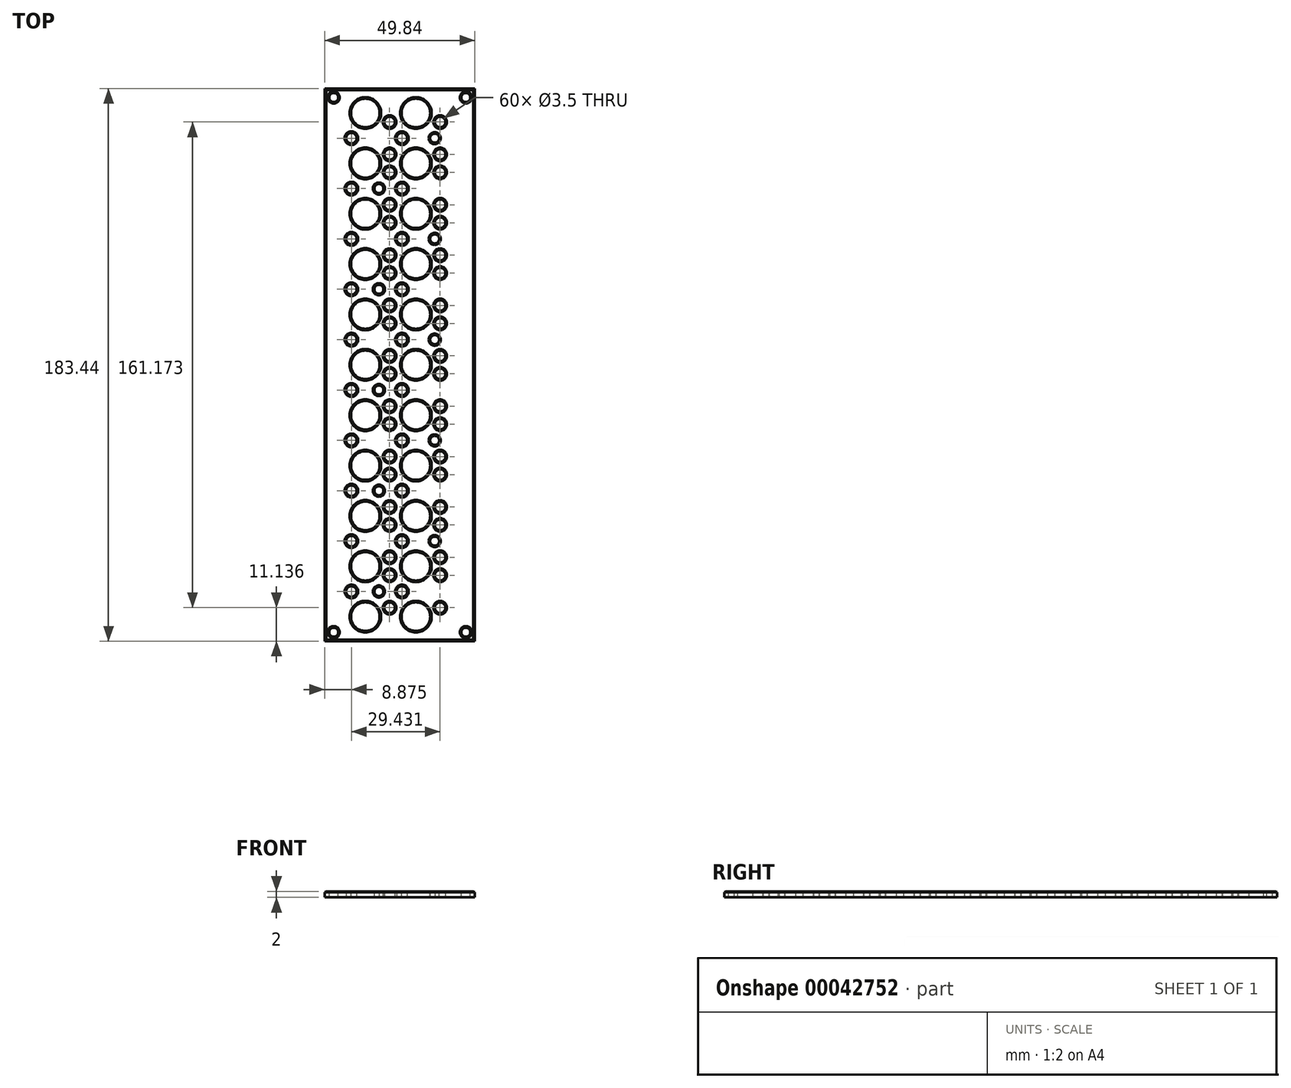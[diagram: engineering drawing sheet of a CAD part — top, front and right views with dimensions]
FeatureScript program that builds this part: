
annotation { "Feature Type Name" : "Feature", "Feature Type Description" : "" }
export const myFeature = defineFeature(function(context is Context, id is Id, definition is map)
    precondition{}
    {
        {
            var Q0;
            Q0=qCreatedBy(makeId("Top.planeOp"),FACE);
            var sketch = newSketch(context, id + "F0", { "sketchPlane" : qUnion([Q0])});
            skLineSegment(sketch, "E0.right", {"start": v(46.84, -3) * mm, "end": v(46.84, 180.44) * mm});
            skLineSegment(sketch, "E0.left", {"start": v(-3, -3) * mm, "end": v(-3, 180.44) * mm});
            skLineSegment(sketch, "E0.top", {"start": v(-3, 180.44) * mm, "end": v(46.84, 180.44) * mm});
            skLineSegment(sketch, "E0.bottom", {"start": v(-3, -3) * mm, "end": v(46.84, -3) * mm});
            skPoint(sketch, "E1.rect.middle", {"position": v(5.88, 30.23) * mm});
            skPoint(sketch, "E2.rect.middle", {"position": v(35.3, 8.14) * mm});
            skPoint(sketch, "E3.rect.middle", {"position": v(35.3, 24.85) * mm});
            skPoint(sketch, "E4.rect.middle", {"position": v(18.54, 24.85) * mm});
            skPoint(sketch, "E5.rect.middle", {"position": v(35.3, 18.89) * mm});
            skPoint(sketch, "E6.rect.middle", {"position": v(22.64, 13.51) * mm});
            skPoint(sketch, "E7.rect.middle", {"position": v(35.3, 35.6) * mm});
            skPoint(sketch, "E8.rect.middle", {"position": v(18.54, 8.14) * mm});
            skPoint(sketch, "E9.rect.middle", {"position": v(18.54, 35.6) * mm});
            skPoint(sketch, "E10.rect.middle", {"position": v(5.88, 13.51) * mm});
            skPoint(sketch, "E11.rect.middle", {"position": v(22.64, 30.23) * mm});
            skPoint(sketch, "E12.rect.middle", {"position": v(18.54, 18.89) * mm});
            skCircle(sketch, "E13", {"center": v(5.88, 13.51) * mm, "radius": 1.75 * mm});
            skCircle(sketch, "E14", {"center": v(18.54, 8.14) * mm, "radius": 1.75 * mm});
            skCircle(sketch, "E15", {"center": v(18.54, 18.89) * mm, "radius": 1.75 * mm});
            skCircle(sketch, "E16", {"center": v(22.64, 13.51) * mm, "radius": 1.75 * mm});
            skCircle(sketch, "E17", {"center": v(35.3, 8.14) * mm, "radius": 1.75 * mm});
            skCircle(sketch, "E18", {"center": v(35.3, 18.89) * mm, "radius": 1.75 * mm});
            skCircle(sketch, "E19", {"center": v(35.3, 24.85) * mm, "radius": 1.75 * mm});
            skCircle(sketch, "E20", {"center": v(35.3, 35.6) * mm, "radius": 1.75 * mm});
            skCircle(sketch, "E21", {"center": v(22.64, 30.23) * mm, "radius": 1.75 * mm});
            skCircle(sketch, "E22", {"center": v(18.54, 35.6) * mm, "radius": 1.75 * mm});
            skCircle(sketch, "E23", {"center": v(18.54, 24.85) * mm, "radius": 1.75 * mm});
            skCircle(sketch, "E24", {"center": v(5.88, 30.23) * mm, "radius": 1.75 * mm});
            skPoint(sketch, "E25.rect.middle", {"position": v(18.54, 69.03) * mm});
            skPoint(sketch, "E26.rect.middle", {"position": v(35.3, 41.56) * mm});
            skPoint(sketch, "E27.rect.middle", {"position": v(35.3, 52.32) * mm});
            skPoint(sketch, "E28.rect.middle", {"position": v(5.88, 46.94) * mm});
            skPoint(sketch, "E29.rect.middle", {"position": v(18.54, 52.32) * mm});
            skPoint(sketch, "E30.rect.middle", {"position": v(35.3, 69.03) * mm});
            skPoint(sketch, "E31.rect.middle", {"position": v(18.54, 41.56) * mm});
            skPoint(sketch, "E32.rect.middle", {"position": v(5.88, 63.65) * mm});
            skPoint(sketch, "E33.rect.middle", {"position": v(35.3, 58.28) * mm});
            skPoint(sketch, "E34.rect.middle", {"position": v(18.54, 58.28) * mm});
            skCircle(sketch, "E35", {"center": v(18.54, 41.56) * mm, "radius": 1.75 * mm});
            skCircle(sketch, "E36", {"center": v(35.3, 41.56) * mm, "radius": 1.75 * mm});
            skCircle(sketch, "E37", {"center": v(35.3, 52.32) * mm, "radius": 1.75 * mm});
            skCircle(sketch, "E38", {"center": v(35.3, 69.03) * mm, "radius": 1.75 * mm});
            skPoint(sketch, "E39.rect.middle", {"position": v(22.64, 63.65) * mm});
            skCircle(sketch, "E40", {"center": v(18.54, 69.03) * mm, "radius": 1.75 * mm});
            skPoint(sketch, "E41.rect.middle", {"position": v(22.64, 46.94) * mm});
            skCircle(sketch, "E42", {"center": v(18.54, 58.28) * mm, "radius": 1.75 * mm});
            skCircle(sketch, "E43", {"center": v(5.88, 63.65) * mm, "radius": 1.75 * mm});
            skCircle(sketch, "E44", {"center": v(5.88, 46.94) * mm, "radius": 1.75 * mm});
            skCircle(sketch, "E45", {"center": v(18.54, 52.32) * mm, "radius": 1.75 * mm});
            skCircle(sketch, "E46", {"center": v(35.3, 58.28) * mm, "radius": 1.75 * mm});
            skCircle(sketch, "E47", {"center": v(22.64, 63.65) * mm, "radius": 1.75 * mm});
            skCircle(sketch, "E48", {"center": v(22.64, 46.94) * mm, "radius": 1.75 * mm});
            skCircle(sketch, "E49", {"center": v(18.54, 135.88) * mm, "radius": 1.75 * mm});
            skPoint(sketch, "E50.rect.middle", {"position": v(35.3, 74.99) * mm});
            skPoint(sketch, "E51.rect.middle", {"position": v(22.64, 130.5) * mm});
            skPoint(sketch, "E52.rect.middle", {"position": v(35.3, 135.88) * mm});
            skPoint(sketch, "E53.rect.middle", {"position": v(5.88, 80.37) * mm});
            skCircle(sketch, "E54", {"center": v(18.54, 125.13) * mm, "radius": 1.75 * mm});
            skCircle(sketch, "E55", {"center": v(18.54, 119.17) * mm, "radius": 1.75 * mm});
            skCircle(sketch, "E56", {"center": v(35.3, 108.42) * mm, "radius": 1.75 * mm});
            skPoint(sketch, "E57.rect.middle", {"position": v(35.3, 125.13) * mm});
            skCircle(sketch, "E58", {"center": v(35.3, 125.13) * mm, "radius": 1.75 * mm});
            skCircle(sketch, "E59", {"center": v(35.3, 119.17) * mm, "radius": 1.75 * mm});
            skCircle(sketch, "E60", {"center": v(35.3, 74.99) * mm, "radius": 1.75 * mm});
            skPoint(sketch, "E61.rect.middle", {"position": v(5.88, 97.08) * mm});
            skCircle(sketch, "E62", {"center": v(22.64, 80.37) * mm, "radius": 1.75 * mm});
            skCircle(sketch, "E63", {"center": v(18.54, 85.74) * mm, "radius": 1.75 * mm});
            skPoint(sketch, "E64.rect.middle", {"position": v(18.54, 102.46) * mm});
            skPoint(sketch, "E65.rect.middle", {"position": v(22.64, 113.8) * mm});
            skCircle(sketch, "E66", {"center": v(18.54, 74.99) * mm, "radius": 1.75 * mm});
            skCircle(sketch, "E67", {"center": v(18.54, 91.7) * mm, "radius": 1.75 * mm});
            skCircle(sketch, "E68", {"center": v(5.88, 80.37) * mm, "radius": 1.75 * mm});
            skCircle(sketch, "E69", {"center": v(5.88, 97.08) * mm, "radius": 1.75 * mm});
            skPoint(sketch, "E70.rect.middle", {"position": v(35.3, 102.46) * mm});
            skCircle(sketch, "E71", {"center": v(18.54, 102.46) * mm, "radius": 1.75 * mm});
            skCircle(sketch, "E72", {"center": v(35.3, 135.88) * mm, "radius": 1.75 * mm});
            skCircle(sketch, "E73", {"center": v(22.64, 130.5) * mm, "radius": 1.75 * mm});
            skPoint(sketch, "E74.rect.middle", {"position": v(5.88, 113.8) * mm});
            skCircle(sketch, "E75", {"center": v(35.3, 85.74) * mm, "radius": 1.75 * mm});
            skPoint(sketch, "E76.rect.middle", {"position": v(18.54, 108.42) * mm});
            skPoint(sketch, "E77.rect.middle", {"position": v(22.64, 97.08) * mm});
            skCircle(sketch, "E78", {"center": v(5.88, 130.5) * mm, "radius": 1.75 * mm});
            skPoint(sketch, "E79.rect.middle", {"position": v(35.3, 91.7) * mm});
            skCircle(sketch, "E80", {"center": v(35.3, 91.7) * mm, "radius": 1.75 * mm});
            skCircle(sketch, "E81", {"center": v(35.3, 102.46) * mm, "radius": 1.75 * mm});
            skCircle(sketch, "E82", {"center": v(22.64, 97.08) * mm, "radius": 1.75 * mm});
            skCircle(sketch, "E83", {"center": v(22.64, 113.8) * mm, "radius": 1.75 * mm});
            skCircle(sketch, "E84", {"center": v(5.88, 113.8) * mm, "radius": 1.75 * mm});
            skCircle(sketch, "E85", {"center": v(18.54, 108.42) * mm, "radius": 1.75 * mm});
            skPoint(sketch, "E86.rect.middle", {"position": v(5.88, 147.22) * mm});
            skPoint(sketch, "E87.rect.middle", {"position": v(18.54, 152.6) * mm});
            skPoint(sketch, "E88.rect.middle", {"position": v(35.3, 169.3) * mm});
            skPoint(sketch, "E89.rect.middle", {"position": v(35.3, 141.84) * mm});
            skPoint(sketch, "E90.rect.middle", {"position": v(18.54, 141.84) * mm});
            skPoint(sketch, "E91.rect.middle", {"position": v(18.54, 169.3) * mm});
            skPoint(sketch, "E92.rect.middle", {"position": v(35.3, 152.6) * mm});
            skPoint(sketch, "E93.rect.middle", {"position": v(18.54, 158.56) * mm});
            skPoint(sketch, "E94.rect.middle", {"position": v(35.3, 158.56) * mm});
            skPoint(sketch, "E95.rect.middle", {"position": v(5.88, 163.93) * mm});
            skCircle(sketch, "E96", {"center": v(35.3, 141.84) * mm, "radius": 1.75 * mm});
            skCircle(sketch, "E97", {"center": v(35.3, 169.3) * mm, "radius": 1.75 * mm});
            skCircle(sketch, "E98", {"center": v(5.88, 163.93) * mm, "radius": 1.75 * mm});
            skCircle(sketch, "E99", {"center": v(18.54, 158.56) * mm, "radius": 1.75 * mm});
            skCircle(sketch, "E100", {"center": v(35.3, 158.56) * mm, "radius": 1.75 * mm});
            skCircle(sketch, "E101", {"center": v(35.3, 152.6) * mm, "radius": 1.75 * mm});
            skCircle(sketch, "E102", {"center": v(18.54, 169.3) * mm, "radius": 1.75 * mm});
            skCircle(sketch, "E103", {"center": v(5.88, 147.22) * mm, "radius": 1.75 * mm});
            skPoint(sketch, "E104.rect.middle", {"position": v(22.64, 147.22) * mm});
            skCircle(sketch, "E105", {"center": v(18.54, 152.6) * mm, "radius": 1.75 * mm});
            skCircle(sketch, "E106", {"center": v(18.54, 141.84) * mm, "radius": 1.75 * mm});
            skPoint(sketch, "E107.rect.middle", {"position": v(22.64, 163.93) * mm});
            skCircle(sketch, "E108", {"center": v(22.64, 147.22) * mm, "radius": 1.75 * mm});
            skCircle(sketch, "E109", {"center": v(22.64, 163.93) * mm, "radius": 1.75 * mm});
            skSolve(sketch);
        }
        {
            var Q0;
            Q0=qSketchRegion(id+"F0",true);
            extrude(context, id + "F1", {"entities" : qUnion([Q0]), "depth" : 2 * mm});
        }
        {
            var Q0;
            Q0=makeQuery(id+"F1.opExtrude","CAP_FACE",FACE,{"disambiguationData":[OSD([sQuery(id+"F0.wireOp",EDGE,"E0.right"),sQuery(id+"F0.wireOp",EDGE,"E0.left"),sQuery(id+"F0.wireOp",EDGE,"E0.top"),sQuery(id+"F0.wireOp",EDGE,"E0.bottom"),sQuery(id+"F0.wireOp",EDGE,"E13"),sQuery(id+"F0.wireOp",EDGE,"E14"),sQuery(id+"F0.wireOp",EDGE,"E15"),sQuery(id+"F0.wireOp",EDGE,"E16"),sQuery(id+"F0.wireOp",EDGE,"E17"),sQuery(id+"F0.wireOp",EDGE,"E18"),sQuery(id+"F0.wireOp",EDGE,"E19"),sQuery(id+"F0.wireOp",EDGE,"E20"),sQuery(id+"F0.wireOp",EDGE,"E21"),sQuery(id+"F0.wireOp",EDGE,"E22"),sQuery(id+"F0.wireOp",EDGE,"E23"),sQuery(id+"F0.wireOp",EDGE,"E24"),sQuery(id+"F0.wireOp",EDGE,"E35"),sQuery(id+"F0.wireOp",EDGE,"E36"),sQuery(id+"F0.wireOp",EDGE,"E37"),sQuery(id+"F0.wireOp",EDGE,"E38"),sQuery(id+"F0.wireOp",EDGE,"E40"),sQuery(id+"F0.wireOp",EDGE,"E42"),sQuery(id+"F0.wireOp",EDGE,"E43"),sQuery(id+"F0.wireOp",EDGE,"E44"),sQuery(id+"F0.wireOp",EDGE,"E45"),sQuery(id+"F0.wireOp",EDGE,"E46"),sQuery(id+"F0.wireOp",EDGE,"E47"),sQuery(id+"F0.wireOp",EDGE,"E48"),sQuery(id+"F0.wireOp",EDGE,"E49"),sQuery(id+"F0.wireOp",EDGE,"E54"),sQuery(id+"F0.wireOp",EDGE,"E55"),sQuery(id+"F0.wireOp",EDGE,"E56"),sQuery(id+"F0.wireOp",EDGE,"E58"),sQuery(id+"F0.wireOp",EDGE,"E59"),sQuery(id+"F0.wireOp",EDGE,"E60"),sQuery(id+"F0.wireOp",EDGE,"E62"),sQuery(id+"F0.wireOp",EDGE,"E63"),sQuery(id+"F0.wireOp",EDGE,"E66"),sQuery(id+"F0.wireOp",EDGE,"E67"),sQuery(id+"F0.wireOp",EDGE,"E68"),sQuery(id+"F0.wireOp",EDGE,"E69"),sQuery(id+"F0.wireOp",EDGE,"E71"),sQuery(id+"F0.wireOp",EDGE,"E72"),sQuery(id+"F0.wireOp",EDGE,"E73"),sQuery(id+"F0.wireOp",EDGE,"E75"),sQuery(id+"F0.wireOp",EDGE,"E78"),sQuery(id+"F0.wireOp",EDGE,"E80"),sQuery(id+"F0.wireOp",EDGE,"E81"),sQuery(id+"F0.wireOp",EDGE,"E82"),sQuery(id+"F0.wireOp",EDGE,"E83"),sQuery(id+"F0.wireOp",EDGE,"E84"),sQuery(id+"F0.wireOp",EDGE,"E85"),sQuery(id+"F0.wireOp",EDGE,"E96"),sQuery(id+"F0.wireOp",EDGE,"E97"),sQuery(id+"F0.wireOp",EDGE,"E98"),sQuery(id+"F0.wireOp",EDGE,"E99"),sQuery(id+"F0.wireOp",EDGE,"E100"),sQuery(id+"F0.wireOp",EDGE,"E101"),sQuery(id+"F0.wireOp",EDGE,"E102"),sQuery(id+"F0.wireOp",EDGE,"E103"),sQuery(id+"F0.wireOp",EDGE,"E105"),sQuery(id+"F0.wireOp",EDGE,"E106"),sQuery(id+"F0.wireOp",EDGE,"E108"),sQuery(id+"F0.wireOp",EDGE,"E109")])],"isStart":false});
            var sketch = newSketch(context, id + "F2", { "sketchPlane" : qUnion([Q0])});
            skCircle(sketch, "E110", {"center": v(10.5, 21.87) * mm, "radius": 4.75 * mm});
            skCircle(sketch, "E111", {"center": v(10.5, 138.86) * mm, "radius": 4.75 * mm});
            skCircle(sketch, "E112", {"center": v(27.26, 155.58) * mm, "radius": 4.75 * mm});
            skCircle(sketch, "E113", {"center": v(27.26, 122.15) * mm, "radius": 4.75 * mm});
            skCircle(sketch, "E114", {"center": v(27.26, 38.58) * mm, "radius": 4.75 * mm});
            skCircle(sketch, "E115", {"center": v(10.5, 155.58) * mm, "radius": 4.75 * mm});
            skCircle(sketch, "E116", {"center": v(10.5, 105.44) * mm, "radius": 4.75 * mm});
            skCircle(sketch, "E117", {"center": v(27.26, 105.44) * mm, "radius": 4.75 * mm});
            skCircle(sketch, "E118", {"center": v(10.5, 88.72) * mm, "radius": 4.75 * mm});
            skCircle(sketch, "E119", {"center": v(27.26, 88.72) * mm, "radius": 4.75 * mm});
            skCircle(sketch, "E120", {"center": v(10.5, 122.15) * mm, "radius": 4.75 * mm});
            skCircle(sketch, "E121", {"center": v(27.26, 172.29) * mm, "radius": 4.75 * mm});
            skCircle(sketch, "E122", {"center": v(10.5, 5.16) * mm, "radius": 4.75 * mm});
            skCircle(sketch, "E123", {"center": v(27.26, 5.16) * mm, "radius": 4.75 * mm});
            skCircle(sketch, "E124", {"center": v(27.26, 21.87) * mm, "radius": 4.75 * mm});
            skCircle(sketch, "E125", {"center": v(27.26, 55.3) * mm, "radius": 4.75 * mm});
            skCircle(sketch, "E126", {"center": v(10.5, 38.58) * mm, "radius": 4.75 * mm});
            skCircle(sketch, "E127", {"center": v(10.5, 172.29) * mm, "radius": 4.75 * mm});
            skCircle(sketch, "E128", {"center": v(27.26, 72) * mm, "radius": 4.75 * mm});
            skCircle(sketch, "E129", {"center": v(10.5, 55.3) * mm, "radius": 4.75 * mm});
            skCircle(sketch, "E130", {"center": v(27.26, 138.86) * mm, "radius": 4.75 * mm});
            skCircle(sketch, "E131", {"center": v(10.5, 72) * mm, "radius": 4.75 * mm});
            skCircle(sketch, "E132", {"center": v(43.84, 0) * mm, "radius": 1.5 * mm});
            skCircle(sketch, "E133", {"center": v(0, 177.44) * mm, "radius": 1.5 * mm});
            skCircle(sketch, "E134", {"center": v(15, 13.51) * mm, "radius": 1.5 * mm});
            skCircle(sketch, "E135", {"center": v(33.5, 30.23) * mm, "radius": 1.5 * mm});
            skCircle(sketch, "E136", {"center": v(15, 46.94) * mm, "radius": 1.5 * mm});
            skCircle(sketch, "E137", {"center": v(33.5, 63.65) * mm, "radius": 1.5 * mm});
            skCircle(sketch, "E138", {"center": v(15, 80.37) * mm, "radius": 1.5 * mm});
            skCircle(sketch, "E139", {"center": v(33.5, 97.08) * mm, "radius": 1.5 * mm});
            skCircle(sketch, "E140", {"center": v(15, 113.8) * mm, "radius": 1.5 * mm});
            skCircle(sketch, "E141", {"center": v(33.5, 130.5) * mm, "radius": 1.5 * mm});
            skCircle(sketch, "E142", {"center": v(33.5, 163.93) * mm, "radius": 1.5 * mm});
            skCircle(sketch, "E143", {"center": v(15, 147.22) * mm, "radius": 1.5 * mm});
            skCircle(sketch, "E144", {"center": v(0, 0) * mm, "radius": 1.5 * mm});
            skCircle(sketch, "E145", {"center": v(43.84, 177.44) * mm, "radius": 1.5 * mm});
            skSolve(sketch);
        }
        {
            var Q0;
            Q0=qSketchRegion(id+"F2",true);
            extrude(context, id + "F3", {"entities" : qUnion([Q0]), "operationType" : NewBodyOperationType.REMOVE, "oppositeDirection" : true, "depth" : 25 * mm});
        }
        {
            var Q0;
            Q0=makeQuery(id+"F1.opExtrude","CAP_FACE",FACE,{"disambiguationData":[OSD([sQuery(id+"F0.wireOp",EDGE,"E0.right"),sQuery(id+"F0.wireOp",EDGE,"E0.left"),sQuery(id+"F0.wireOp",EDGE,"E0.top"),sQuery(id+"F0.wireOp",EDGE,"E0.bottom"),sQuery(id+"F0.wireOp",EDGE,"E13"),sQuery(id+"F0.wireOp",EDGE,"E14"),sQuery(id+"F0.wireOp",EDGE,"E15"),sQuery(id+"F0.wireOp",EDGE,"E16"),sQuery(id+"F0.wireOp",EDGE,"E17"),sQuery(id+"F0.wireOp",EDGE,"E18"),sQuery(id+"F0.wireOp",EDGE,"E19"),sQuery(id+"F0.wireOp",EDGE,"E20"),sQuery(id+"F0.wireOp",EDGE,"E21"),sQuery(id+"F0.wireOp",EDGE,"E22"),sQuery(id+"F0.wireOp",EDGE,"E23"),sQuery(id+"F0.wireOp",EDGE,"E24"),sQuery(id+"F0.wireOp",EDGE,"E35"),sQuery(id+"F0.wireOp",EDGE,"E36"),sQuery(id+"F0.wireOp",EDGE,"E37"),sQuery(id+"F0.wireOp",EDGE,"E38"),sQuery(id+"F0.wireOp",EDGE,"E40"),sQuery(id+"F0.wireOp",EDGE,"E42"),sQuery(id+"F0.wireOp",EDGE,"E43"),sQuery(id+"F0.wireOp",EDGE,"E44"),sQuery(id+"F0.wireOp",EDGE,"E45"),sQuery(id+"F0.wireOp",EDGE,"E46"),sQuery(id+"F0.wireOp",EDGE,"E47"),sQuery(id+"F0.wireOp",EDGE,"E48"),sQuery(id+"F0.wireOp",EDGE,"E49"),sQuery(id+"F0.wireOp",EDGE,"E54"),sQuery(id+"F0.wireOp",EDGE,"E55"),sQuery(id+"F0.wireOp",EDGE,"E56"),sQuery(id+"F0.wireOp",EDGE,"E58"),sQuery(id+"F0.wireOp",EDGE,"E59"),sQuery(id+"F0.wireOp",EDGE,"E60"),sQuery(id+"F0.wireOp",EDGE,"E62"),sQuery(id+"F0.wireOp",EDGE,"E63"),sQuery(id+"F0.wireOp",EDGE,"E66"),sQuery(id+"F0.wireOp",EDGE,"E67"),sQuery(id+"F0.wireOp",EDGE,"E68"),sQuery(id+"F0.wireOp",EDGE,"E69"),sQuery(id+"F0.wireOp",EDGE,"E71"),sQuery(id+"F0.wireOp",EDGE,"E72"),sQuery(id+"F0.wireOp",EDGE,"E73"),sQuery(id+"F0.wireOp",EDGE,"E75"),sQuery(id+"F0.wireOp",EDGE,"E78"),sQuery(id+"F0.wireOp",EDGE,"E80"),sQuery(id+"F0.wireOp",EDGE,"E81"),sQuery(id+"F0.wireOp",EDGE,"E82"),sQuery(id+"F0.wireOp",EDGE,"E83"),sQuery(id+"F0.wireOp",EDGE,"E84"),sQuery(id+"F0.wireOp",EDGE,"E85"),sQuery(id+"F0.wireOp",EDGE,"E96"),sQuery(id+"F0.wireOp",EDGE,"E97"),sQuery(id+"F0.wireOp",EDGE,"E98"),sQuery(id+"F0.wireOp",EDGE,"E99"),sQuery(id+"F0.wireOp",EDGE,"E100"),sQuery(id+"F0.wireOp",EDGE,"E101"),sQuery(id+"F0.wireOp",EDGE,"E102"),sQuery(id+"F0.wireOp",EDGE,"E103"),sQuery(id+"F0.wireOp",EDGE,"E105"),sQuery(id+"F0.wireOp",EDGE,"E106"),sQuery(id+"F0.wireOp",EDGE,"E108"),sQuery(id+"F0.wireOp",EDGE,"E109")])],"isStart":false});
            chamfer(context, id + "F4", {"entities" : qUnion([Q0]), "chamferType" : ChamferType.OFFSET_ANGLE, "width" : .5 * mm, "oppositeDirection" : false, "angle" : 30 * degree, "tangentPropagation" : true});
        }
    });
